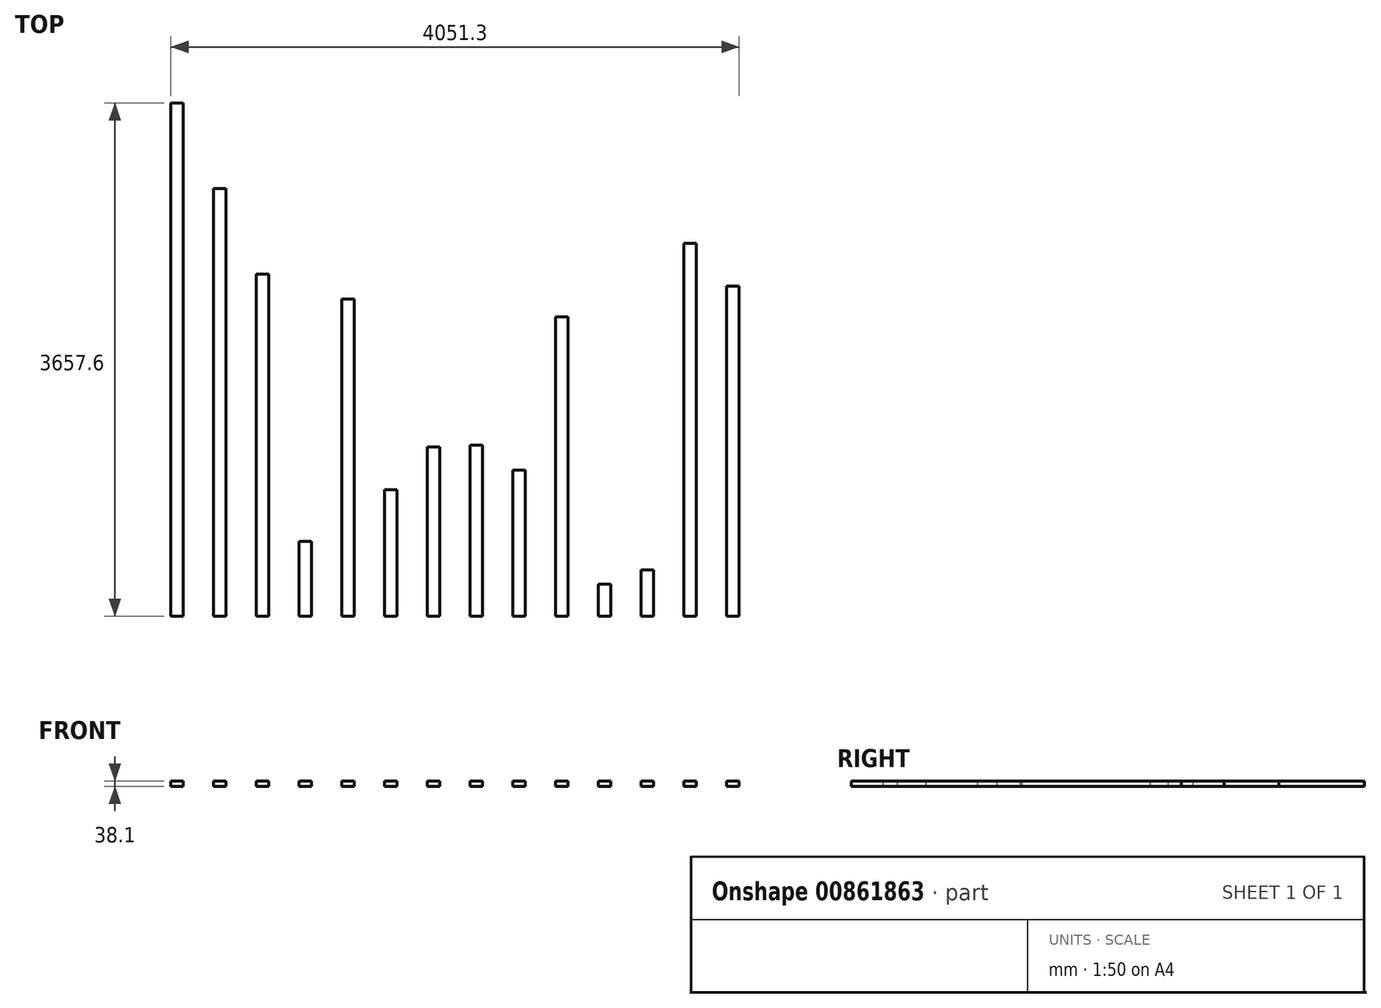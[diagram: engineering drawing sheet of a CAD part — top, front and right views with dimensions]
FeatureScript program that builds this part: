
annotation { "Feature Type Name" : "Feature", "Feature Type Description" : "" }
export const myFeature = defineFeature(function(context is Context, id is Id, definition is map)
    precondition{}
    {
        {
            var Q0;
            Q0=qCreatedBy(makeId("Front.planeOp"),FACE);
            var sketch = newSketch(context, id + "F0", { "sketchPlane" : qUnion([Q0])});
            skLineSegment(sketch, "E0.bottom", {"start": v(44.45, -19.05) * mm, "end": v(-44.45, -19.05) * mm});
            skLineSegment(sketch, "E0.top", {"start": v(44.45, 19.05) * mm, "end": v(-44.45, 19.05) * mm});
            skLineSegment(sketch, "E0.left", {"start": v(44.45, -19.05) * mm, "end": v(44.45, 19.05) * mm});
            skLineSegment(sketch, "E0.right", {"start": v(-44.45, -19.05) * mm, "end": v(-44.45, 19.05) * mm});
            skPoint(sketch, "E0.middle", {"position": v(0, 0) * mm});
            skSolve(sketch);
        }
        {
            var Q0;
            Q0=makeQuery(id+"F0.imprint","IMPRINT",FACE,{"disambiguationData":[TD([[makeQuery(id+"F0.imprint","IMPRINT",EDGE,{"derivedFrom":sQuery(id+"F0.wireOp",EDGE,"E0.bottom")}),-1.0]])]});
            extrude(context, id + "F1", {"entities" : qUnion([Q0]), "depth" : 2438.4 * mm});
        }
        {
            var Q0;
            Q0=makeQuery(id+"F1.opExtrude","SWEPT_BODY",BODY,{"disambiguationData":[OSD([sQuery(id+"F0.wireOp",EDGE,"E0.bottom"),sQuery(id+"F0.wireOp",EDGE,"E0.top"),sQuery(id+"F0.wireOp",EDGE,"E0.left"),sQuery(id+"F0.wireOp",EDGE,"E0.right")])]});
            transform(context, id + "F2", {"entities" : qUnion([Q0]), "transformType" : TransformType.TRANSLATION_3D, "dx" : 304.8 * mm, "dy" : 0 * mm, "dz" : 0 * mm, "makeCopy" : true});
        }
        {
            var Q0;
            Q0=makeQuery(id+"F2.opPattern","COPY",FACE,{"derivedFrom":makeQuery(id+"F1.opExtrude","CAP_FACE",FACE,{"disambiguationData":[OSD([sQuery(id+"F0.wireOp",EDGE,"E0.bottom"),sQuery(id+"F0.wireOp",EDGE,"E0.top"),sQuery(id+"F0.wireOp",EDGE,"E0.left"),sQuery(id+"F0.wireOp",EDGE,"E0.right")])],"isStart":true}),"instanceName":"1"});
            extrude(context, id + "F3", {"entities" : qUnion([Q0]), "operationType" : NewBodyOperationType.REMOVE, "oppositeDirection" : true, "depth" : 1905 * mm});
        }
        {
            var Q0;
            Q0=makeQuery(id+"F1.opExtrude","SWEPT_BODY",BODY,{"disambiguationData":[OSD([sQuery(id+"F0.wireOp",EDGE,"E0.bottom"),sQuery(id+"F0.wireOp",EDGE,"E0.top"),sQuery(id+"F0.wireOp",EDGE,"E0.left"),sQuery(id+"F0.wireOp",EDGE,"E0.right")])]});
            transform(context, id + "F4", {"entities" : qUnion([Q0]), "transformType" : TransformType.TRANSLATION_3D, "dx" : -304.8 * mm, "dy" : 0 * mm, "dz" : 0 * mm, "makeCopy" : true});
        }
        {
            var Q0;
            Q0=makeQuery(id+"F4.opPattern","COPY",FACE,{"derivedFrom":makeQuery(id+"F1.opExtrude","CAP_FACE",FACE,{"disambiguationData":[OSD([sQuery(id+"F0.wireOp",EDGE,"E0.bottom"),sQuery(id+"F0.wireOp",EDGE,"E0.top"),sQuery(id+"F0.wireOp",EDGE,"E0.left"),sQuery(id+"F0.wireOp",EDGE,"E0.right")])],"isStart":true}),"instanceName":"1"});
            extrude(context, id + "F5", {"entities" : qUnion([Q0]), "operationType" : NewBodyOperationType.ADD, "depth" : 609.6 * mm});
        }
        {
            var Q0;
            Q0=makeQuery(id+"F4.opPattern","COPY",BODY,{"derivedFrom":makeQuery(id+"F1.opExtrude","SWEPT_BODY",BODY,{"disambiguationData":[OSD([sQuery(id+"F0.wireOp",EDGE,"E0.bottom"),sQuery(id+"F0.wireOp",EDGE,"E0.top"),sQuery(id+"F0.wireOp",EDGE,"E0.left"),sQuery(id+"F0.wireOp",EDGE,"E0.right")])]}),"instanceName":"1"});
            transform(context, id + "F6", {"entities" : qUnion([Q0]), "transformType" : TransformType.TRANSLATION_3D, "dx" : -304.8 * mm, "dy" : 0 * mm, "dz" : 0 * mm, "makeCopy" : true});
        }
        {
            var Q0;
            Q0=makeQuery(id+"F6.opPattern","COPY",FACE,{"derivedFrom":makeQuery(id+"F5.opExtrude","CAP_FACE",FACE,{"disambiguationData":[OSD([sQuery(id+"F0.wireOp",EDGE,"E0.bottom"),sQuery(id+"F0.wireOp",EDGE,"E0.top"),sQuery(id+"F0.wireOp",EDGE,"E0.left"),sQuery(id+"F0.wireOp",EDGE,"E0.right")])],"isStart":false}),"instanceName":"1"});
            extrude(context, id + "F7", {"entities" : qUnion([Q0]), "operationType" : NewBodyOperationType.ADD, "depth" : 609.6 * mm});
        }
        {
            var Q0;
            Q0=makeQuery(id+"F1.opExtrude","SWEPT_BODY",BODY,{"disambiguationData":[OSD([sQuery(id+"F0.wireOp",EDGE,"E0.bottom"),sQuery(id+"F0.wireOp",EDGE,"E0.top"),sQuery(id+"F0.wireOp",EDGE,"E0.left"),sQuery(id+"F0.wireOp",EDGE,"E0.right")])]});
            transform(context, id + "F8", {"entities" : qUnion([Q0]), "transformType" : TransformType.TRANSLATION_3D, "dx" : 609.6 * mm, "dy" : 0 * mm, "dz" : 0 * mm, "makeCopy" : true});
        }
        {
            var Q0;
            Q0=makeQuery(id+"F8.opPattern","COPY",FACE,{"derivedFrom":makeQuery(id+"F1.opExtrude","CAP_FACE",FACE,{"disambiguationData":[OSD([sQuery(id+"F0.wireOp",EDGE,"E0.bottom"),sQuery(id+"F0.wireOp",EDGE,"E0.top"),sQuery(id+"F0.wireOp",EDGE,"E0.left"),sQuery(id+"F0.wireOp",EDGE,"E0.right")])],"isStart":true}),"instanceName":"1"});
            extrude(context, id + "F9", {"entities" : qUnion([Q0]), "operationType" : NewBodyOperationType.ADD, "oppositeDirection" : true, "depth" : 177.8 * mm});
        }
        {
            var Q0;
            Q0=makeQuery(id+"F8.opPattern","COPY",FACE,{"derivedFrom":makeQuery(id+"F1.opExtrude","CAP_FACE",FACE,{"disambiguationData":[OSD([sQuery(id+"F0.wireOp",EDGE,"E0.bottom"),sQuery(id+"F0.wireOp",EDGE,"E0.top"),sQuery(id+"F0.wireOp",EDGE,"E0.left"),sQuery(id+"F0.wireOp",EDGE,"E0.right")])],"isStart":true}),"instanceName":"1"});
            extrude(context, id + "F10", {"entities" : qUnion([Q0]), "operationType" : NewBodyOperationType.REMOVE, "oppositeDirection" : true, "depth" : 177.8 * mm});
        }
        {
            var Q0;
            Q0=makeQuery(id+"F8.opPattern","COPY",BODY,{"derivedFrom":makeQuery(id+"F1.opExtrude","SWEPT_BODY",BODY,{"disambiguationData":[OSD([sQuery(id+"F0.wireOp",EDGE,"E0.bottom"),sQuery(id+"F0.wireOp",EDGE,"E0.top"),sQuery(id+"F0.wireOp",EDGE,"E0.left"),sQuery(id+"F0.wireOp",EDGE,"E0.right")])]}),"instanceName":"1"});
            transform(context, id + "F11", {"entities" : qUnion([Q0]), "transformType" : TransformType.TRANSLATION_3D, "dx" : 304.8 * mm, "dy" : 0 * mm, "dz" : 0 * mm, "makeCopy" : true});
        }
        {
            var Q0;
            Q0=makeQuery(id+"F11.opPattern","COPY",FACE,{"derivedFrom":makeQuery(id+"F10.boolean.opBoolean","COPY",FACE,{"derivedFrom":makeQuery(id+"F10.opExtrude","CAP_FACE",FACE,{"disambiguationData":[OSD([sQuery(id+"F0.wireOp",EDGE,"E0.bottom"),sQuery(id+"F0.wireOp",EDGE,"E0.top"),sQuery(id+"F0.wireOp",EDGE,"E0.left"),sQuery(id+"F0.wireOp",EDGE,"E0.right")])],"isStart":false})}),"instanceName":"1"});
            extrude(context, id + "F12", {"entities" : qUnion([Q0]), "operationType" : NewBodyOperationType.REMOVE, "oppositeDirection" : true, "depth" : 1536.7 * mm});
        }
        {
            var Q0;
            Q0=makeQuery(id+"F12.boolean.opBoolean","COPY",FACE,{"derivedFrom":makeQuery(id+"F12.opExtrude","CAP_FACE",FACE,{"disambiguationData":[OSD([sQuery(id+"F0.wireOp",EDGE,"E0.bottom"),sQuery(id+"F0.wireOp",EDGE,"E0.top"),sQuery(id+"F0.wireOp",EDGE,"E0.left"),sQuery(id+"F0.wireOp",EDGE,"E0.right")])],"isStart":false})});
            extrude(context, id + "F13", {"entities" : qUnion([Q0]), "operationType" : NewBodyOperationType.ADD, "depth" : 177.8 * mm});
        }
        {
            var Q0;
            Q0=makeQuery(id+"F11.opPattern","COPY",BODY,{"derivedFrom":makeQuery(id+"F8.opPattern","COPY",BODY,{"derivedFrom":makeQuery(id+"F1.opExtrude","SWEPT_BODY",BODY,{"disambiguationData":[OSD([sQuery(id+"F0.wireOp",EDGE,"E0.bottom"),sQuery(id+"F0.wireOp",EDGE,"E0.top"),sQuery(id+"F0.wireOp",EDGE,"E0.left"),sQuery(id+"F0.wireOp",EDGE,"E0.right")])]}),"instanceName":"1"}),"instanceName":"1"});
            transform(context, id + "F14", {"entities" : qUnion([Q0]), "transformType" : TransformType.TRANSLATION_3D, "dx" : 304.8 * mm, "dy" : 0 * mm, "dz" : 0 * mm, "makeCopy" : true});
        }
        {
            var Q0;
            Q0=makeQuery(id+"F14.opPattern","COPY",FACE,{"derivedFrom":makeQuery(id+"F13.opExtrude","CAP_FACE",FACE,{"disambiguationData":[OSD([sQuery(id+"F0.wireOp",EDGE,"E0.bottom"),sQuery(id+"F0.wireOp",EDGE,"E0.top"),sQuery(id+"F0.wireOp",EDGE,"E0.left"),sQuery(id+"F0.wireOp",EDGE,"E0.right")])],"isStart":false}),"instanceName":"1"});
            extrude(context, id + "F15", {"entities" : qUnion([Q0]), "operationType" : NewBodyOperationType.ADD, "depth" : 304.8 * mm});
        }
        {
            var Q0;
            Q0=makeQuery(id+"F1.opExtrude","SWEPT_BODY",BODY,{"disambiguationData":[OSD([sQuery(id+"F0.wireOp",EDGE,"E0.bottom"),sQuery(id+"F0.wireOp",EDGE,"E0.top"),sQuery(id+"F0.wireOp",EDGE,"E0.left"),sQuery(id+"F0.wireOp",EDGE,"E0.right")])]});
            transform(context, id + "F16", {"entities" : qUnion([Q0]), "transformType" : TransformType.TRANSLATION_3D, "dx" : 1524 * mm, "dy" : 0 * mm, "dz" : 0 * mm, "makeCopy" : true});
        }
        {
            var Q0;
            Q0=makeQuery(id+"F16.opPattern","COPY",FACE,{"derivedFrom":makeQuery(id+"F1.opExtrude","CAP_FACE",FACE,{"disambiguationData":[OSD([sQuery(id+"F0.wireOp",EDGE,"E0.bottom"),sQuery(id+"F0.wireOp",EDGE,"E0.top"),sQuery(id+"F0.wireOp",EDGE,"E0.left"),sQuery(id+"F0.wireOp",EDGE,"E0.right")])],"isStart":true}),"instanceName":"1"});
            extrude(context, id + "F17", {"entities" : qUnion([Q0]), "operationType" : NewBodyOperationType.REMOVE, "oppositeDirection" : true, "depth" : 1219.2 * mm});
        }
        {
            var Q0;
            Q0=makeQuery(id+"F16.opPattern","COPY",BODY,{"derivedFrom":makeQuery(id+"F1.opExtrude","SWEPT_BODY",BODY,{"disambiguationData":[OSD([sQuery(id+"F0.wireOp",EDGE,"E0.bottom"),sQuery(id+"F0.wireOp",EDGE,"E0.top"),sQuery(id+"F0.wireOp",EDGE,"E0.left"),sQuery(id+"F0.wireOp",EDGE,"E0.right")])]}),"instanceName":"1"});
            transform(context, id + "F18", {"entities" : qUnion([Q0]), "transformType" : TransformType.TRANSLATION_3D, "dx" : 304.8 * mm, "dy" : 0 * mm, "dz" : 0 * mm, "makeCopy" : true});
        }
        {
            var Q0;
            Q0=makeQuery(id+"F18.opPattern","COPY",FACE,{"derivedFrom":makeQuery(id+"F17.boolean.opBoolean","COPY",FACE,{"derivedFrom":makeQuery(id+"F17.opExtrude","CAP_FACE",FACE,{"disambiguationData":[OSD([sQuery(id+"F0.wireOp",EDGE,"E0.bottom"),sQuery(id+"F0.wireOp",EDGE,"E0.top"),sQuery(id+"F0.wireOp",EDGE,"E0.left"),sQuery(id+"F0.wireOp",EDGE,"E0.right")])],"isStart":false})}),"instanceName":"1"});
            extrude(context, id + "F19", {"entities" : qUnion([Q0]), "operationType" : NewBodyOperationType.REMOVE, "oppositeDirection" : true, "depth" : 177.8 * mm});
        }
        {
            var Q0;
            Q0=makeQuery(id+"F18.opPattern","COPY",BODY,{"derivedFrom":makeQuery(id+"F16.opPattern","COPY",BODY,{"derivedFrom":makeQuery(id+"F1.opExtrude","SWEPT_BODY",BODY,{"disambiguationData":[OSD([sQuery(id+"F0.wireOp",EDGE,"E0.bottom"),sQuery(id+"F0.wireOp",EDGE,"E0.top"),sQuery(id+"F0.wireOp",EDGE,"E0.left"),sQuery(id+"F0.wireOp",EDGE,"E0.right")])]}),"instanceName":"1"}),"instanceName":"1"});
            transform(context, id + "F20", {"entities" : qUnion([Q0]), "transformType" : TransformType.TRANSLATION_3D, "dx" : 304.8 * mm, "dy" : 0 * mm, "dz" : 0 * mm, "makeCopy" : true});
        }
        {
            var Q0;
            Q0=makeQuery(id+"F20.opPattern","COPY",FACE,{"derivedFrom":makeQuery(id+"F19.boolean.opBoolean","COPY",FACE,{"derivedFrom":makeQuery(id+"F19.opExtrude","CAP_FACE",FACE,{"disambiguationData":[OSD([sQuery(id+"F0.wireOp",EDGE,"E0.bottom"),sQuery(id+"F0.wireOp",EDGE,"E0.top"),sQuery(id+"F0.wireOp",EDGE,"E0.left"),sQuery(id+"F0.wireOp",EDGE,"E0.right")])],"isStart":false})}),"instanceName":"1"});
            extrude(context, id + "F21", {"entities" : qUnion([Q0]), "operationType" : NewBodyOperationType.ADD, "depth" : 1092.2 * mm});
        }
        {
            var Q0;
            Q0=makeQuery(id+"F20.opPattern","COPY",BODY,{"derivedFrom":makeQuery(id+"F18.opPattern","COPY",BODY,{"derivedFrom":makeQuery(id+"F16.opPattern","COPY",BODY,{"derivedFrom":makeQuery(id+"F1.opExtrude","SWEPT_BODY",BODY,{"disambiguationData":[OSD([sQuery(id+"F0.wireOp",EDGE,"E0.bottom"),sQuery(id+"F0.wireOp",EDGE,"E0.top"),sQuery(id+"F0.wireOp",EDGE,"E0.left"),sQuery(id+"F0.wireOp",EDGE,"E0.right")])]}),"instanceName":"1"}),"instanceName":"1"}),"instanceName":"1"});
            transform(context, id + "F22", {"entities" : qUnion([Q0]), "transformType" : TransformType.TRANSLATION_3D, "dx" : 304.8 * mm, "dy" : 0 * mm, "dz" : 0 * mm, "makeCopy" : true});
        }
        {
            var Q0;
            Q0=makeQuery(id+"F22.opPattern","COPY",FACE,{"derivedFrom":makeQuery(id+"F21.opExtrude","CAP_FACE",FACE,{"disambiguationData":[OSD([sQuery(id+"F0.wireOp",EDGE,"E0.bottom"),sQuery(id+"F0.wireOp",EDGE,"E0.top"),sQuery(id+"F0.wireOp",EDGE,"E0.left"),sQuery(id+"F0.wireOp",EDGE,"E0.right")])],"isStart":false}),"instanceName":"1"});
            extrude(context, id + "F23", {"entities" : qUnion([Q0]), "operationType" : NewBodyOperationType.REMOVE, "oppositeDirection" : true, "depth" : 1828.8 * mm});
        }
        {
            var Q0;
            Q0=makeQuery(id+"F23.boolean.opBoolean","COPY",FACE,{"derivedFrom":makeQuery(id+"F23.opExtrude","CAP_FACE",FACE,{"disambiguationData":[OSD([sQuery(id+"F0.wireOp",EDGE,"E0.bottom"),sQuery(id+"F0.wireOp",EDGE,"E0.top"),sQuery(id+"F0.wireOp",EDGE,"E0.left"),sQuery(id+"F0.wireOp",EDGE,"E0.right")])],"isStart":false})});
            extrude(context, id + "F24", {"entities" : qUnion([Q0]), "operationType" : NewBodyOperationType.REMOVE, "oppositeDirection" : true, "depth" : 76.2 * mm});
        }
        {
            var Q0;
            Q0=makeQuery(id+"F22.opPattern","COPY",BODY,{"derivedFrom":makeQuery(id+"F20.opPattern","COPY",BODY,{"derivedFrom":makeQuery(id+"F18.opPattern","COPY",BODY,{"derivedFrom":makeQuery(id+"F16.opPattern","COPY",BODY,{"derivedFrom":makeQuery(id+"F1.opExtrude","SWEPT_BODY",BODY,{"disambiguationData":[OSD([sQuery(id+"F0.wireOp",EDGE,"E0.bottom"),sQuery(id+"F0.wireOp",EDGE,"E0.top"),sQuery(id+"F0.wireOp",EDGE,"E0.left"),sQuery(id+"F0.wireOp",EDGE,"E0.right")])]}),"instanceName":"1"}),"instanceName":"1"}),"instanceName":"1"}),"instanceName":"1"});
            transform(context, id + "F25", {"entities" : qUnion([Q0]), "transformType" : TransformType.TRANSLATION_3D, "dx" : 304.8 * mm, "dy" : 0 * mm, "dz" : 0 * mm, "makeCopy" : true});
        }
        {
            var Q0;
            Q0=makeQuery(id+"F25.opPattern","COPY",FACE,{"derivedFrom":makeQuery(id+"F24.boolean.opBoolean","COPY",FACE,{"derivedFrom":makeQuery(id+"F24.opExtrude","CAP_FACE",FACE,{"disambiguationData":[OSD([sQuery(id+"F0.wireOp",EDGE,"E0.bottom"),sQuery(id+"F0.wireOp",EDGE,"E0.top"),sQuery(id+"F0.wireOp",EDGE,"E0.left"),sQuery(id+"F0.wireOp",EDGE,"E0.right")])],"isStart":false})}),"instanceName":"1"});
            extrude(context, id + "F26", {"entities" : qUnion([Q0]), "operationType" : NewBodyOperationType.ADD, "depth" : 101.6 * mm});
        }
        {
            var Q0;
            Q0=makeQuery(id+"F25.opPattern","COPY",BODY,{"derivedFrom":makeQuery(id+"F22.opPattern","COPY",BODY,{"derivedFrom":makeQuery(id+"F20.opPattern","COPY",BODY,{"derivedFrom":makeQuery(id+"F18.opPattern","COPY",BODY,{"derivedFrom":makeQuery(id+"F16.opPattern","COPY",BODY,{"derivedFrom":makeQuery(id+"F1.opExtrude","SWEPT_BODY",BODY,{"disambiguationData":[OSD([sQuery(id+"F0.wireOp",EDGE,"E0.bottom"),sQuery(id+"F0.wireOp",EDGE,"E0.top"),sQuery(id+"F0.wireOp",EDGE,"E0.left"),sQuery(id+"F0.wireOp",EDGE,"E0.right")])]}),"instanceName":"1"}),"instanceName":"1"}),"instanceName":"1"}),"instanceName":"1"}),"instanceName":"1"});
            transform(context, id + "F27", {"entities" : qUnion([Q0]), "transformType" : TransformType.TRANSLATION_3D, "dx" : 304.8 * mm, "dy" : 0 * mm, "dz" : 0 * mm, "makeCopy" : true});
        }
        {
            var Q0;
            Q0=makeQuery(id+"F27.opPattern","COPY",FACE,{"derivedFrom":makeQuery(id+"F26.opExtrude","CAP_FACE",FACE,{"disambiguationData":[OSD([sQuery(id+"F0.wireOp",EDGE,"E0.bottom"),sQuery(id+"F0.wireOp",EDGE,"E0.top"),sQuery(id+"F0.wireOp",EDGE,"E0.left"),sQuery(id+"F0.wireOp",EDGE,"E0.right")])],"isStart":false}),"instanceName":"1"});
            extrude(context, id + "F28", {"entities" : qUnion([Q0]), "operationType" : NewBodyOperationType.ADD, "depth" : 2327.28 * mm});
        }
        {
            var Q0;
            Q0=makeQuery(id+"F27.opPattern","COPY",BODY,{"derivedFrom":makeQuery(id+"F25.opPattern","COPY",BODY,{"derivedFrom":makeQuery(id+"F22.opPattern","COPY",BODY,{"derivedFrom":makeQuery(id+"F20.opPattern","COPY",BODY,{"derivedFrom":makeQuery(id+"F18.opPattern","COPY",BODY,{"derivedFrom":makeQuery(id+"F16.opPattern","COPY",BODY,{"derivedFrom":makeQuery(id+"F1.opExtrude","SWEPT_BODY",BODY,{"disambiguationData":[OSD([sQuery(id+"F0.wireOp",EDGE,"E0.bottom"),sQuery(id+"F0.wireOp",EDGE,"E0.top"),sQuery(id+"F0.wireOp",EDGE,"E0.left"),sQuery(id+"F0.wireOp",EDGE,"E0.right")])]}),"instanceName":"1"}),"instanceName":"1"}),"instanceName":"1"}),"instanceName":"1"}),"instanceName":"1"}),"instanceName":"1"});
            transform(context, id + "F29", {"entities" : qUnion([Q0]), "transformType" : TransformType.TRANSLATION_3D, "dx" : 304.8 * mm, "dy" : 0 * mm, "dz" : 0 * mm, "makeCopy" : true});
        }
        {
            var Q0;
            Q0=makeQuery(id+"F29.opPattern","COPY",FACE,{"derivedFrom":makeQuery(id+"F28.opExtrude","CAP_FACE",FACE,{"disambiguationData":[OSD([sQuery(id+"F0.wireOp",EDGE,"E0.bottom"),sQuery(id+"F0.wireOp",EDGE,"E0.top"),sQuery(id+"F0.wireOp",EDGE,"E0.left"),sQuery(id+"F0.wireOp",EDGE,"E0.right")])],"isStart":false}),"instanceName":"1"});
            extrude(context, id + "F30", {"entities" : qUnion([Q0]), "operationType" : NewBodyOperationType.REMOVE, "oppositeDirection" : true, "depth" : 304.8 * mm});
        }
    });
